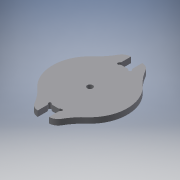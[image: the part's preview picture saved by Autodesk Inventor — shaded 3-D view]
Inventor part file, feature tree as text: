
AUTODESK INVENTOR PART (.ipt)
format: ipt  version: 2016 (Build 200138000, 138)  size: 159,232 bytes
history: native  units: mm
features: fillet x2, extrude x1, sketch x1
ambient origin geometry x8: Origin, YZ Plane, XZ Plane, XY Plane, X Axis, Y Axis, Z Axis, Center Point
bodies: Solid1 (feature_tree)
feature tree (4):
  extrude  "Extrusion1"  Depth=30.0mm
  fillet  "Fillet1"  Radius=5.0mm
  fillet  "Fillet2"  Radius=3.0mm
  sketch  "Sketch1"  dims[d0=3.0mm d1=31.75mm d4=5.0mm d5=3.0mm d6=3.0mm d8=20.0mm d9=40.0mm d10=0.75mm d11=3.0mm d12=0.0mm d13=1.0mm d14=5.0mm d15=30.0mm]
